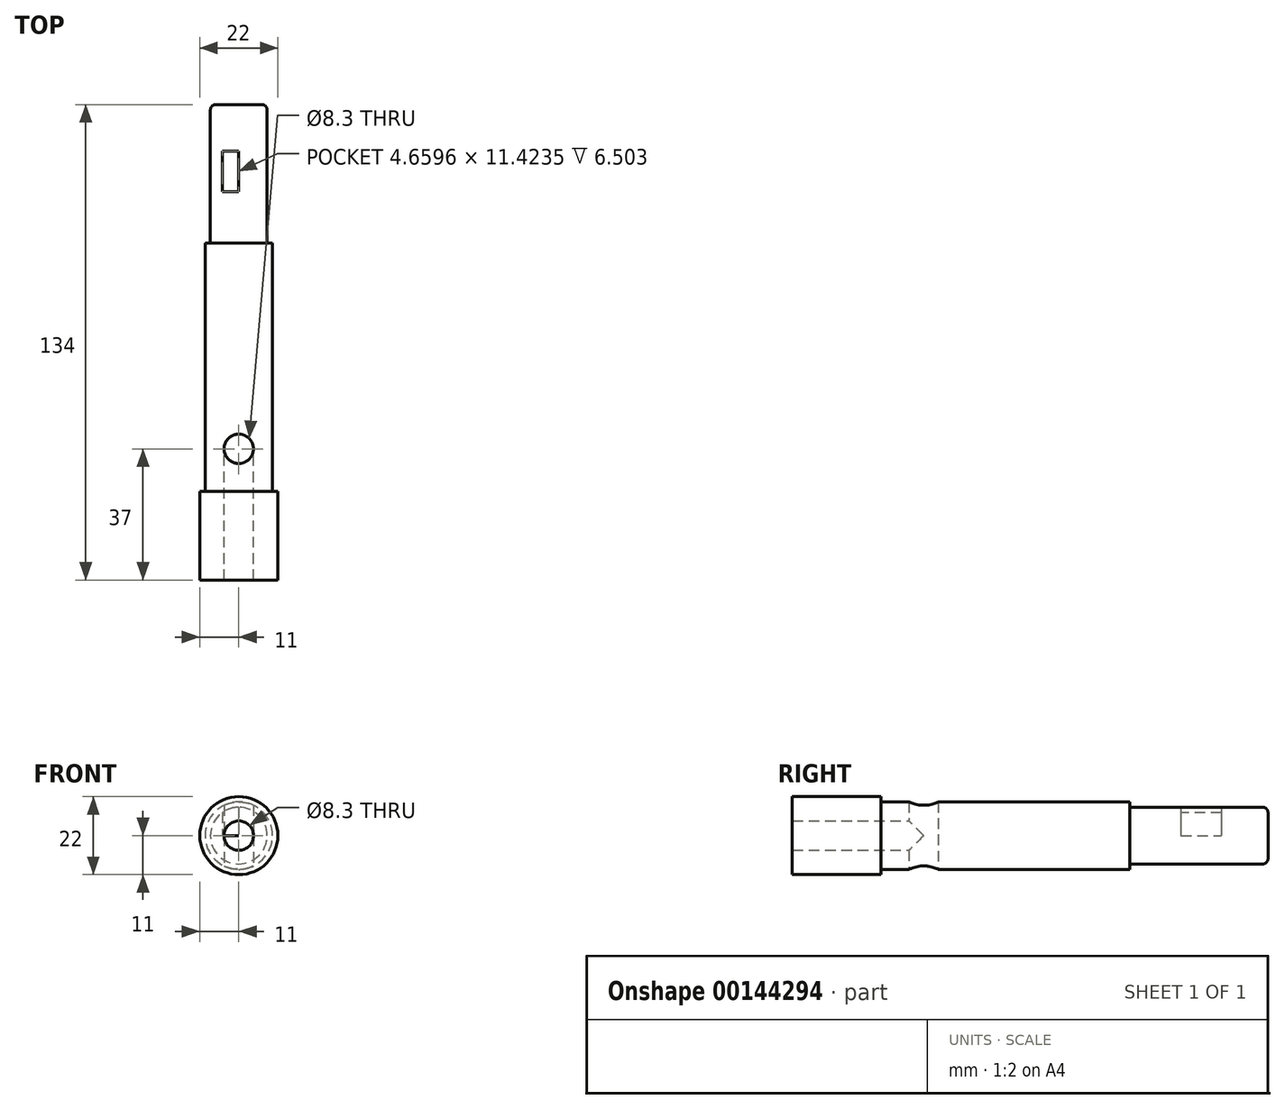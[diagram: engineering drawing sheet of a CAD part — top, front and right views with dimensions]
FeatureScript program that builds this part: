
annotation { "Feature Type Name" : "Feature", "Feature Type Description" : "" }
export const myFeature = defineFeature(function(context is Context, id is Id, definition is map)
    precondition{}
    {
        {
            var Q0;
            Q0=qCreatedBy(makeId("Front.planeOp"),FACE);
            var sketch = newSketch(context, id + "F0", { "sketchPlane" : qUnion([Q0])});
            skCircle(sketch, "E0", {"center": v(0, 0) * mm, "radius": 11 * mm});
            skCircle(sketch, "E1", {"center": v(0, 0) * mm, "radius": 4.15 * mm});
            skSolve(sketch);
        }
        {
            var Q0;
            Q0=makeQuery(id+"F0.imprint","IMPRINT",FACE,{"disambiguationData":[TD([[makeQuery(id+"F0.imprint","IMPRINT",EDGE,{"derivedFrom":sQuery(id+"F0.wireOp",EDGE,"E0")}),1.0]])]});
            extrude(context, id + "F1", {"entities" : qUnion([Q0]), "depth" : 25 * mm});
        }
        {
            var Q0;
            Q0=makeQuery(id+"F1.opExtrude","CAP_FACE",FACE,{"disambiguationData":[OSD([sQuery(id+"F0.wireOp",EDGE,"E0"),sQuery(id+"F0.wireOp",EDGE,"E1")])],"isStart":true});
            var sketch = newSketch(context, id + "F2", { "sketchPlane" : qUnion([Q0])});
            skCircle(sketch, "E2", {"center": v(0, 0) * mm, "radius": 9.5 * mm});
            skSolve(sketch);
        }
        {
            var Q0;
            Q0=makeQuery(id+"F2.imprint","IMPRINT",FACE,{"disambiguationData":[TD([[makeQuery(id+"F2.imprint","IMPRINT",EDGE,{"derivedFrom":sQuery(id+"F2.wireOp",EDGE,"E2")}),1.0]])]});
            var Q1;
            Q1=makeQuery(id+"F2.imprint","IMPRINT",FACE,{"disambiguationData":[TD([[makeQuery(id+"F2.imprint","IMPRINT",EDGE,{"derivedFrom":makeQuery(id+"F1.opExtrude","CAP_EDGE",EDGE,{"disambiguationData":[OSD([sQuery(id+"F0.wireOp",EDGE,"E1")])],"isStart":true})}),-1.0]])]});
            extrude(context, id + "F3", {"entities" : qUnion([Q0, Q1]), "operationType" : NewBodyOperationType.ADD, "depth" : 70 * mm});
        }
        {
            var Q0;
            Q0=qCreatedBy(makeId("Top.planeOp"),FACE);
            var sketch = newSketch(context, id + "F4", { "sketchPlane" : qUnion([Q0])});
            skLineSegment(sketch, "E3", {"start": v(0, 0) * mm, "end": v(0, 12) * mm, "construction": true});
            skCircle(sketch, "E4", {"center": v(0, 12) * mm, "radius": 4.15 * mm});
            skSolve(sketch);
        }
        {
            var Q0;
            Q0 = qSketchRegion(id + "F4", true);
            extrude(context, id + "F5", {"entities" : qUnion([Q0]), "operationType" : NewBodyOperationType.REMOVE, "endBound" : BoundingType.THROUGH_ALL, "depth" : 25 * mm, "hasSecondDirection" : true, "secondDirectionOppositeDirection" : true, "secondDirectionDepth" : 25 * mm});
        }
        {
            var Q0;
            Q0=makeQuery(id+"F1.opExtrude","CAP_FACE",FACE,{"disambiguationData":[OSD([sQuery(id+"F0.wireOp",EDGE,"E0"),sQuery(id+"F0.wireOp",EDGE,"E1")])],"isStart":false});
            var sketch = newSketch(context, id + "F6", { "sketchPlane" : qUnion([Q0])});
            skCircle(sketch, "E5", {"center": v(0, 0) * mm, "radius": 4.15 * mm});
            skSolve(sketch);
        }
        {
            var Q0;
            Q0=makeQuery(id+"F6.imprint","IMPRINT",FACE,{"disambiguationData":[TD([[makeQuery(id+"F6.imprint","IMPRINT",EDGE,{"derivedFrom":sQuery(id+"F6.wireOp",EDGE,"E5")}),1.0]])]});
            extrude(context, id + "F7", {"entities" : qUnion([Q0]), "operationType" : NewBodyOperationType.REMOVE, "oppositeDirection" : true, "depth" : 37 * mm});
        }
        {
            var Q0;
            Q0=makeQuery(id+"F3.opExtrude","CAP_FACE",FACE,{"disambiguationData":[OSD([sQuery(id+"F2.wireOp",EDGE,"E2")])],"isStart":false});
            var sketch = newSketch(context, id + "F8", { "sketchPlane" : qUnion([Q0])});
            skCircle(sketch, "E6", {"center": v(0, 0) * mm, "radius": 8 * mm});
            skSolve(sketch);
        }
        {
            var Q0;
            Q0=makeQuery(id+"F8.imprint","IMPRINT",FACE,{"disambiguationData":[TD([[makeQuery(id+"F8.imprint","IMPRINT",EDGE,{"derivedFrom":sQuery(id+"F8.wireOp",EDGE,"E6")}),1.0]])]});
            extrude(context, id + "F9", {"entities" : qUnion([Q0]), "operationType" : NewBodyOperationType.ADD, "depth" : 39 * mm});
        }
        {
            var Q0;
            Q0=makeQuery(id+"F9.opExtrude","CAP_EDGE",EDGE,{"disambiguationData":[OSD([sQuery(id+"F8.wireOp",EDGE,"E6")])],"isStart":false});
            fillet(context, id + "F10", {"entities" : qUnion([Q0]), "radius" : 1.5 * mm, "tangentPropagation" : true, "allowEdgeOverflow" : false});
        }
        {
            var Q0;
            Q0=qCreatedBy(makeId("Top.planeOp"),FACE);
            var sketch = newSketch(context, id + "F11", { "sketchPlane" : qUnion([Q0])});
            skLineSegment(sketch, "E7.bottom", {"start": v(0, 84.47) * mm, "end": v(-4.66, 84.47) * mm});
            skLineSegment(sketch, "E7.top", {"start": v(0, 95.9) * mm, "end": v(-4.66, 95.9) * mm});
            skLineSegment(sketch, "E7.left", {"start": v(0, 84.47) * mm, "end": v(0, 95.9) * mm});
            skLineSegment(sketch, "E7.right", {"start": v(-4.66, 84.47) * mm, "end": v(-4.66, 95.9) * mm});
            skSolve(sketch);
        }
        {
            var Q0;
            Q0 = qSketchRegion(id + "F11", true);
            extrude(context, id + "F12", {"entities" : qUnion([Q0]), "operationType" : NewBodyOperationType.REMOVE, "depth" : 25 * mm});
        }
    });
